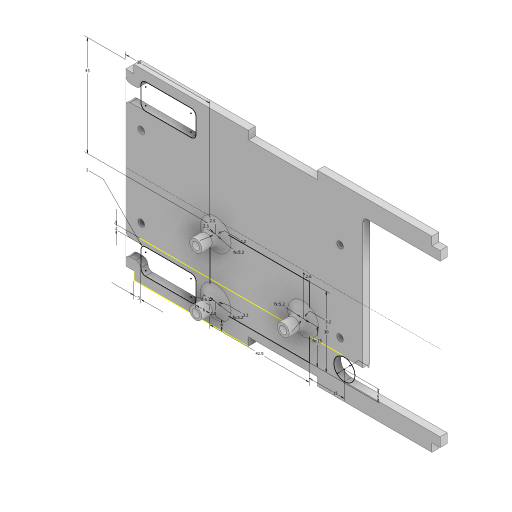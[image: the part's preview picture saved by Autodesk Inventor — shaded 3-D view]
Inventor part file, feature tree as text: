
AUTODESK INVENTOR PART (.ipt)
format: ipt  version: 2023 (Build 270158000, 158)  size: 360,448 bytes
history: native  units: mm
features: extrude x8, sketch x5, fillet x2
ambient origin geometry x8: Origin, YZ Plane, XZ Plane, XY Plane, X Axis, Y Axis, Z Axis, Center Point
bodies: Solid1 (feature_tree)
feature tree (15):
  extrude  "Base Plate"  Depth=80.0mm
  sketch  "Sketch2"  dims[d2=3.5mm d3=3.5mm]
  extrude  "CubePilot Outline"  Depth=3.5mm
  extrude  "Extrusion3"  Depth=3.5mm
  sketch  "Sketch3"  dims[d4=3.5mm d5=3.5mm]
  extrude  "Extrusion4"  Depth=49.0mm
  fillet  "Fillet1"  Radius=3.5mm
  extrude  "Extrusion5"  Depth=3.0mm TaperAngle=0.0deg
  extrude  "Extrusion6"  Depth=44.29mm
  extrude  "Extrusion7"  TaperAngle=0.0deg  [1 undecoded]
  extrude  "Extrusion8"  Depth=94.46mm
  fillet  "Fillet2"  Radius=2.0mm
  sketch  "Sketch1"  dims[d0=134.5mm d1=80.0mm]
  sketch  "Sketch4"  dims[d6=49.0mm d7=49.0mm d8=3.5mm]
  sketch  "Sketch6"  dims[d9=3.5mm d10=3.0mm d11=0.0mm d12=44.29mm d13=0.0mm d14=94.46mm d15=2.0mm d16=4.0mm d17=1.0mm d18=2.8mm d19=20.0mm d21=85.0mm d22=20.0mm d24=34.4mm d27=4.73mm d28=4.945mm d29=0.5mm d30=0.0mm d31=0.0mm d32=0.0mm d33=42.5mm d34=30.0mm d35=43.0mm d36=36.0mm d37=3.2mm d38=3.2mm d39=3.2mm d40=2.5mm d41=2.5mm d42=2.5mm d43=2.5mm d44=2.6mm d45=15.0mm d46=9.0mm d47=5.0mm d48=15.0mm d49=3.0mm d50=4.0mm d51=2.0mm d52=6.0mm d53=2.0mm d54=5.2mm d55=5.2mm d56=5.2mm d57=8.5mm d58=0.0mm d59=4.0mm d60=5.8mm d61=5.8mm d62=5.8mm d63=2.8mm d64=0.0mm d65=0.0mm d66=0.0mm d67=7.5mm d68=7.5mm d69=0.0mm d70=4.0mm d71=2.0mm d72=0.0mm d73=0.0mm d74=12.0mm d75=5.0mm d76=15.0mm d77=15.0mm d78=6.0mm d79=8.0mm d80=2.0mm d81=8.0mm d82=2.0mm d83=0.0mm d84=0.0mm d85=2.0mm]
note: 1 required parameter value undecoded (feature->parameter linkage not recoverable at this tier; creation-order binding heuristic only, values carry confidence <= 0.55)
